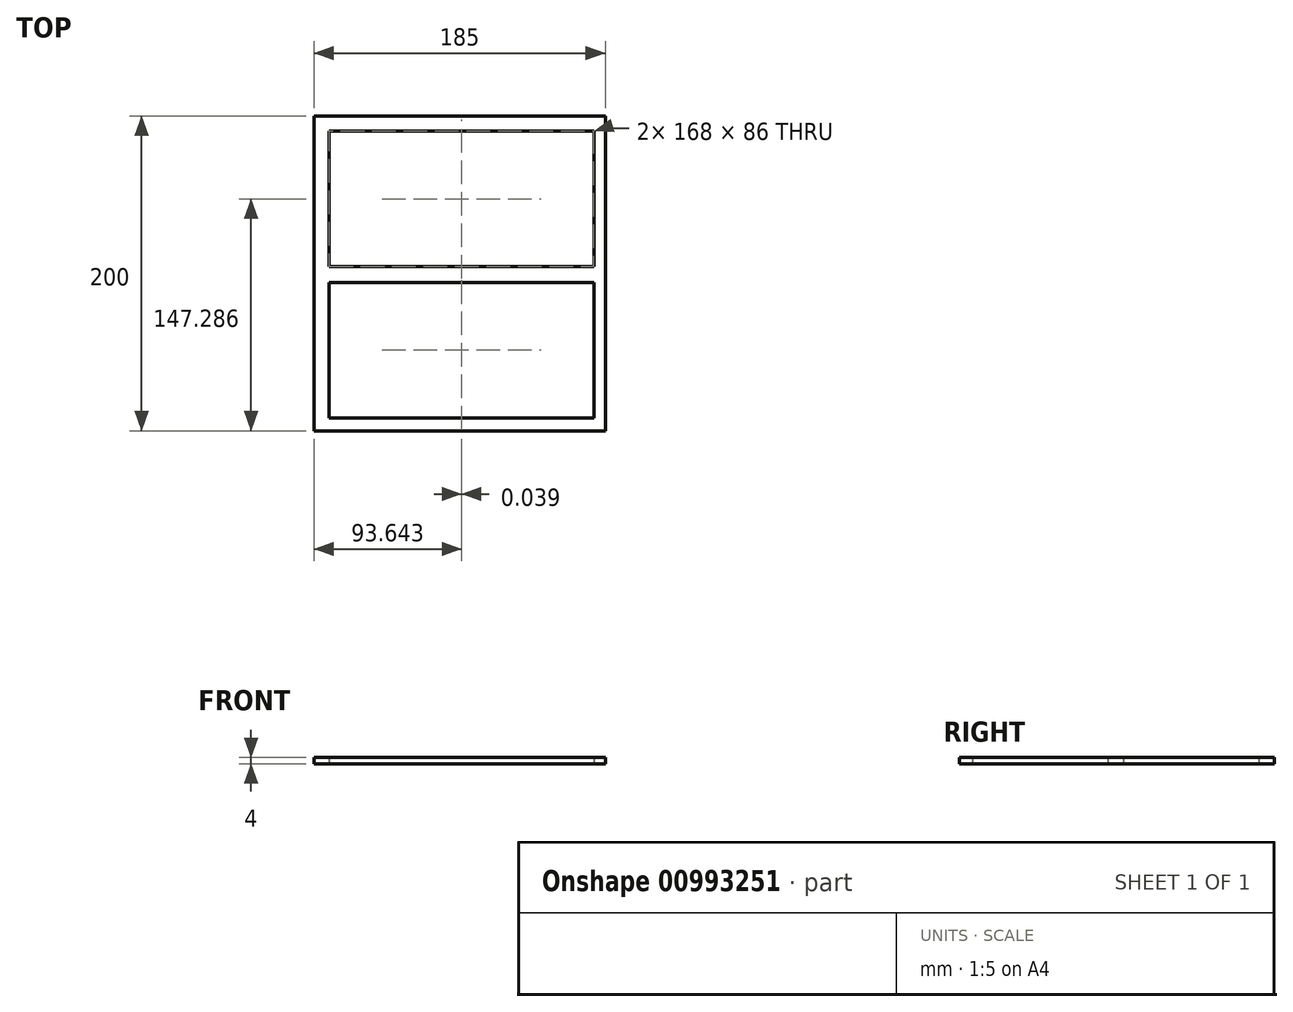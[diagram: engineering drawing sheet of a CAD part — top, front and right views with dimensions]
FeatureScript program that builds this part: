
annotation { "Feature Type Name" : "Feature", "Feature Type Description" : "" }
export const myFeature = defineFeature(function(context is Context, id is Id, definition is map)
    precondition{}
    {
        {
            var Q0;
            Q0=qCreatedBy(makeId("Top.planeOp"),FACE);
            var sketch = newSketch(context, id + "F0", { "sketchPlane" : qUnion([Q0])});
            skLineSegment(sketch, "E0.bottom", {"start": v(-76.5, 84.74) * mm, "end": v(91.5, 84.74) * mm});
            skLineSegment(sketch, "E0.top", {"start": v(-76.5, -1.26) * mm, "end": v(91.5, -1.26) * mm});
            skLineSegment(sketch, "E0.left", {"start": v(-76.5, 84.74) * mm, "end": v(-76.5, -1.26) * mm});
            skLineSegment(sketch, "E0.right", {"start": v(91.5, 84.74) * mm, "end": v(91.5, -1.26) * mm});
            skLineSegment(sketch, "E1.bottom", {"start": v(-76.47, -11.26) * mm, "end": v(91.53, -11.26) * mm});
            skLineSegment(sketch, "E1.top", {"start": v(-76.47, -97.26) * mm, "end": v(91.53, -97.26) * mm});
            skLineSegment(sketch, "E1.left", {"start": v(-76.47, -11.26) * mm, "end": v(-76.47, -97.26) * mm});
            skLineSegment(sketch, "E1.right", {"start": v(91.53, -11.26) * mm, "end": v(91.53, -97.26) * mm});
            skLineSegment(sketch, "E2.bottom", {"start": v(-86.15, 94.45) * mm, "end": v(98.85, 94.45) * mm});
            skLineSegment(sketch, "E2.top", {"start": v(-86.15, -105.55) * mm, "end": v(98.85, -105.55) * mm});
            skLineSegment(sketch, "E2.left", {"start": v(-86.15, 94.45) * mm, "end": v(-86.15, -105.55) * mm});
            skLineSegment(sketch, "E2.right", {"start": v(98.85, 94.45) * mm, "end": v(98.85, -105.55) * mm});
            skSolve(sketch);
        }
        {
            var Q0;
            Q0=makeQuery(id+"F0.imprint","IMPRINT",FACE,{"disambiguationData":[TD([[makeQuery(id+"F0.imprint","IMPRINT",EDGE,{"derivedFrom":sQuery(id+"F0.wireOp",EDGE,"E0.bottom")}),1.0]])]});
            extrude(context, id + "F1", {"entities" : qUnion([Q0]), "depth" : 4 * mm, "offsetDistance" : 25 * mm});
        }
    });
